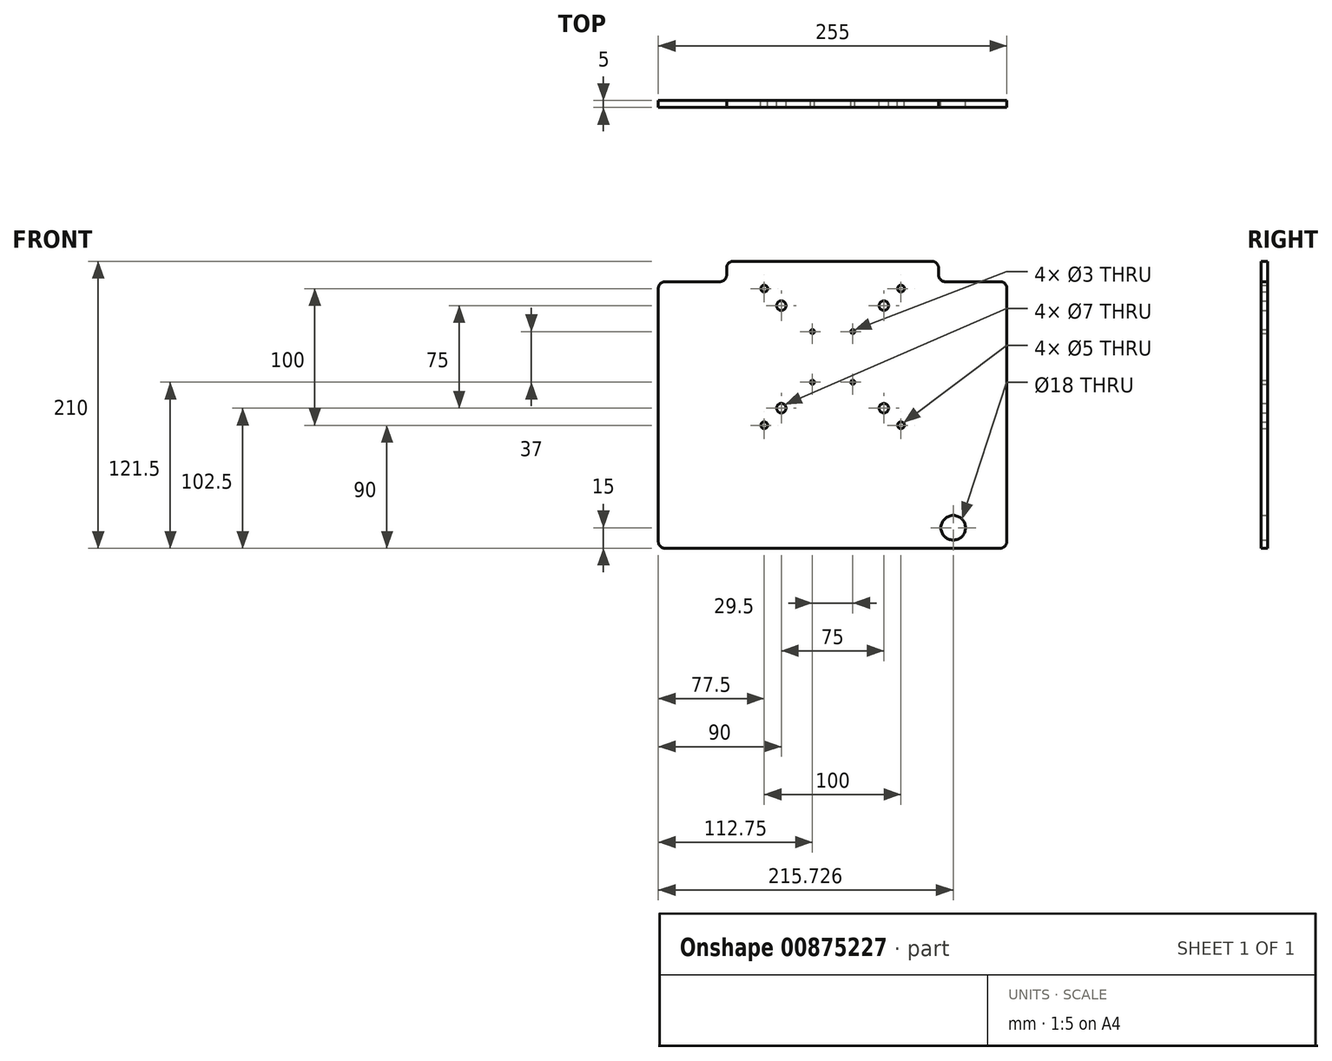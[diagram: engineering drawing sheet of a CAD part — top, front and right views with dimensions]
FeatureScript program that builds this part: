
annotation { "Feature Type Name" : "Feature", "Feature Type Description" : "" }
export const myFeature = defineFeature(function(context is Context, id is Id, definition is map)
    precondition{}
    {
        {
            var Q0;
            Q0=qCreatedBy(makeId("Front.planeOp"),FACE);
            var sketch = newSketch(context, id + "F0", { "sketchPlane" : qUnion([Q0])});
            skLineSegment(sketch, "E0.bottom", {"start": v(122.5, -105) * mm, "end": v(-122.5, -105) * mm});
            skLineSegment(sketch, "E0.top", {"start": v(72.5, 105) * mm, "end": v(-72.5, 105) * mm});
            skLineSegment(sketch, "E0.left", {"start": v(127.5, -100) * mm, "end": v(127.5, 85) * mm});
            skLineSegment(sketch, "E0.right", {"start": v(-127.5, -100) * mm, "end": v(-127.5, 85) * mm});
            skPoint(sketch, "E0.middle", {"position": v(0, 0) * mm});
            skLineSegment(sketch, "E1.bottom", {"start": v(-50, -15) * mm, "end": v(50, -15) * mm});
            skLineSegment(sketch, "E1.top", {"start": v(-50, 85) * mm, "end": v(50, 85) * mm});
            skLineSegment(sketch, "E1.left", {"start": v(-50, -15) * mm, "end": v(-50, 85) * mm});
            skLineSegment(sketch, "E1.right", {"start": v(50, -15) * mm, "end": v(50, 85) * mm});
            skPoint(sketch, "E1.middle", {"position": v(0, 35) * mm});
            skLineSegment(sketch, "E2", {"start": v(0, 85) * mm, "end": v(0, 105) * mm});
            skLineSegment(sketch, "E3.bottom", {"start": v(127.5, 105) * mm, "end": v(77.5, 105) * mm});
            skLineSegment(sketch, "E3.top", {"start": v(122.5, 90) * mm, "end": v(82.5, 90) * mm});
            skLineSegment(sketch, "E3.right", {"start": v(77.5, 100) * mm, "end": v(77.5, 95) * mm});
            skLineSegment(sketch, "E4.bottom", {"start": v(-127.5, 105) * mm, "end": v(-77.5, 105) * mm});
            skLineSegment(sketch, "E4.top", {"start": v(-122.5, 90) * mm, "end": v(-82.5, 90) * mm});
            skLineSegment(sketch, "E4.left", {"start": v(-127.5, 105) * mm, "end": v(-127.5, 90) * mm});
            skLineSegment(sketch, "E4.right", {"start": v(-77.5, 100) * mm, "end": v(-77.5, 95) * mm});
            skPoint(sketch, "E5.visualSharp", {"position": v(127.5, -105) * mm});
            skArc(sketch, "E5.filletArc", {"start": v(122.5, -105) * mm, "mid": v(126.04, -103.54) * mm, "end": v(127.5, -100) * mm});
            skPoint(sketch, "E6.visualSharp", {"position": v(-127.5, -105) * mm});
            skArc(sketch, "E6.filletArc", {"start": v(-127.5, -100) * mm, "mid": v(-126.04, -103.54) * mm, "end": v(-122.5, -105) * mm});
            skCircle(sketch, "E7", {"center": v(50, 85) * mm, "radius": 2.5 * mm});
            skCircle(sketch, "E8", {"center": v(-50, 85) * mm, "radius": 2.5 * mm});
            skCircle(sketch, "E9", {"center": v(-50, -15) * mm, "radius": 2.5 * mm});
            skCircle(sketch, "E10", {"center": v(50, -15) * mm, "radius": 2.5 * mm});
            skCircle(sketch, "E11", {"center": v(88.23, -90) * mm, "radius": 9 * mm});
            skLineSegment(sketch, "E12", {"start": v(88.23, -90) * mm, "end": v(88.23, -105) * mm});
            skPoint(sketch, "E13.newPointA", {"position": v(127.5, 105) * mm});
            skPoint(sketch, "E13.newPointB", {"position": v(127.5, 90) * mm});
            skArc(sketch, "E13.filletArc", {"start": v(127.5, 85) * mm, "mid": v(126.04, 88.54) * mm, "end": v(122.5, 90) * mm});
            skPoint(sketch, "E14.newPointA", {"position": v(77.5, 105) * mm});
            skArc(sketch, "E14.filletArc", {"start": v(77.5, 100) * mm, "mid": v(76.04, 103.54) * mm, "end": v(72.5, 105) * mm});
            skPoint(sketch, "E15.newPointA", {"position": v(-127.5, 105) * mm});
            skPoint(sketch, "E15.newPointB", {"position": v(-77.5, 105) * mm});
            skArc(sketch, "E15.filletArc", {"start": v(-72.5, 105) * mm, "mid": v(-76.04, 103.54) * mm, "end": v(-77.5, 100) * mm});
            skPoint(sketch, "E16.visualSharp", {"position": v(-77.5, 90) * mm});
            skArc(sketch, "E16.filletArc", {"start": v(-82.5, 90) * mm, "mid": v(-78.96, 91.46) * mm, "end": v(-77.5, 95) * mm});
            skPoint(sketch, "E17.visualSharp", {"position": v(77.5, 90) * mm});
            skArc(sketch, "E17.filletArc", {"start": v(77.5, 95) * mm, "mid": v(78.96, 91.46) * mm, "end": v(82.5, 90) * mm});
            skPoint(sketch, "E18.newPointA", {"position": v(-127.5, 90) * mm});
            skArc(sketch, "E18.filletArc", {"start": v(-122.5, 90) * mm, "mid": v(-126.04, 88.54) * mm, "end": v(-127.5, 85) * mm});
            skLineSegment(sketch, "E19.bottom", {"start": v(37.5, -2.5) * mm, "end": v(-37.5, -2.5) * mm});
            skLineSegment(sketch, "E19.top", {"start": v(37.5, 72.5) * mm, "end": v(-37.5, 72.5) * mm});
            skLineSegment(sketch, "E19.left", {"start": v(37.5, -2.5) * mm, "end": v(37.5, 72.5) * mm});
            skLineSegment(sketch, "E19.right", {"start": v(-37.5, -2.5) * mm, "end": v(-37.5, 72.5) * mm});
            skLineSegment(sketch, "E20.bottom", {"start": v(14.75, 16.5) * mm, "end": v(-14.75, 16.5) * mm});
            skLineSegment(sketch, "E20.top", {"start": v(14.75, 53.5) * mm, "end": v(-14.75, 53.5) * mm});
            skLineSegment(sketch, "E20.left", {"start": v(14.75, 16.5) * mm, "end": v(14.75, 53.5) * mm});
            skLineSegment(sketch, "E20.right", {"start": v(-14.75, 16.5) * mm, "end": v(-14.75, 53.5) * mm});
            skCircle(sketch, "E21", {"center": v(-37.5, 72.5) * mm, "radius": 3.5 * mm});
            skCircle(sketch, "E22", {"center": v(-37.5, -2.5) * mm, "radius": 3.5 * mm});
            skCircle(sketch, "E23", {"center": v(37.5, -2.5) * mm, "radius": 3.5 * mm});
            skCircle(sketch, "E24", {"center": v(37.5, 72.5) * mm, "radius": 3.5 * mm});
            skCircle(sketch, "E25", {"center": v(-14.75, 53.5) * mm, "radius": 1.5 * mm});
            skCircle(sketch, "E26", {"center": v(-14.75, 16.5) * mm, "radius": 1.5 * mm});
            skCircle(sketch, "E27", {"center": v(14.75, 16.5) * mm, "radius": 1.5 * mm});
            skCircle(sketch, "E28", {"center": v(14.75, 53.5) * mm, "radius": 1.5 * mm});
            skSolve(sketch);
        }
        {
            var Q0;
            Q0=makeQuery(id+"F0.imprint","IMPRINT",FACE,{"disambiguationData":[TD([[makeQuery(id+"F0.imprint","IMPRINT",EDGE,{"derivedFrom":sQuery(id+"F0.wireOp",EDGE,"E0.right")}),-1.0]])]});
            var Q1;
            {var subQ5=sQuery(id+"F0.wireOp",EDGE,"E1.top");var subQ6=makeQuery(id+"F0.imprint","IMPRINT",VERTEX,{"derivedFrom":subQ5});Q1=makeQuery(id+"F0.imprint","IMPRINT",FACE,{"disambiguationData":[TD([[makeQuery(id+"F0.imprint","IMPRINT",EDGE,{"disambiguationData":[TD([[subQ6,1.0]])],"derivedFrom":subQ5}),-1.0]])]});}
            var Q2;
            {var subQ21=sQuery(id+"F0.wireOp",EDGE,"E23");var subQ22=sQuery(id+"F0.wireOp",EDGE,"E19.bottom");var subQ23=makeQuery(id+"F0.imprint","INTERSECT",VERTEX,{"derivedFrom":[subQ22,subQ21]});Q2=makeQuery(id+"F0.imprint","IMPRINT",FACE,{"disambiguationData":[TD([[makeQuery(id+"F0.imprint","IMPRINT",EDGE,{"disambiguationData":[TD([[subQ23,-1.0]])],"derivedFrom":subQ22}),-1.0]])]});}
            var Q3;
            {var subQ7=sQuery(id+"F0.wireOp",EDGE,"E27");var subQ13=sQuery(id+"F0.wireOp",EDGE,"E20.bottom");var subQ14=makeQuery(id+"F0.imprint","INTERSECT",VERTEX,{"derivedFrom":[subQ13,subQ7]});Q3=makeQuery(id+"F0.imprint","IMPRINT",FACE,{"disambiguationData":[TD([[makeQuery(id+"F0.imprint","IMPRINT",EDGE,{"disambiguationData":[TD([[subQ14,-1.0]])],"derivedFrom":subQ13}),-1.0]])]});}
            extrude(context, id + "F1", {"entities" : qUnion([Q0, Q1, Q2, Q3]), "depth" : 5 * mm, "offsetDistance" : 25 * mm});
        }
    });
